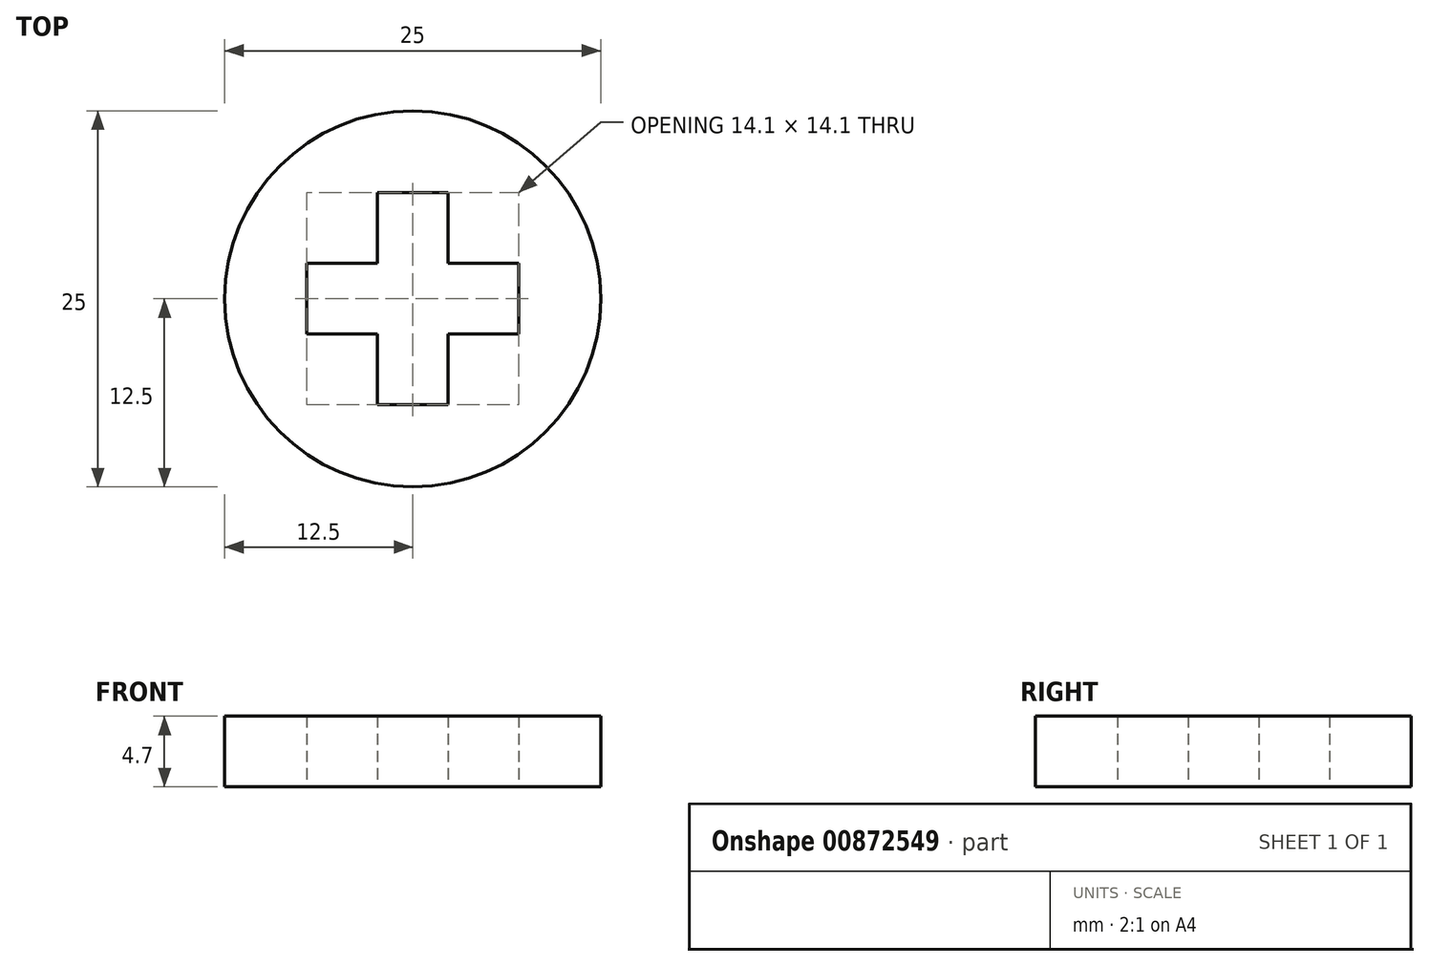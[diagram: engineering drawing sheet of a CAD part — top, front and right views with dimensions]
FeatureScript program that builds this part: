
annotation { "Feature Type Name" : "Feature", "Feature Type Description" : "" }
export const myFeature = defineFeature(function(context is Context, id is Id, definition is map)
    precondition{}
    {
        {
            assignVariable(context, id + "F0", {"name" : "e", "anyValue" : 4.7});
        }
        {
            var Q0;
            Q0=qCreatedBy(makeId("Top.planeOp"),FACE);
            var sketch = newSketch(context, id + "F1", { "sketchPlane" : qUnion([Q0])});
            skCircle(sketch, "E0", {"center": v(0, 0) * mm, "radius": 12.5 * mm});
            skLineSegment(sketch, "E1", {"start": v(-7.05, 2.35) * mm, "end": v(-7.05, -2.35) * mm});
            skLineSegment(sketch, "E2", {"start": v(-31.45, 0) * mm, "end": v(18.7, 0) * mm, "construction": true});
            skPoint(sketch, "E3", {"position": v(-7.05, 0) * mm});
            skLineSegment(sketch, "E4", {"start": v(-7.05, 2.35) * mm, "end": v(-2.35, 2.35) * mm});
            skLineSegment(sketch, "E5", {"start": v(-2.35, 2.35) * mm, "end": v(-2.35, 7.05) * mm});
            skLineSegment(sketch, "E6", {"start": v(-2.35, 7.05) * mm, "end": v(2.35, 7.05) * mm});
            skLineSegment(sketch, "E7", {"start": v(2.35, 7.05) * mm, "end": v(2.35, 2.35) * mm});
            skLineSegment(sketch, "E8", {"start": v(2.35, 2.35) * mm, "end": v(7.05, 2.35) * mm});
            skLineSegment(sketch, "E9", {"start": v(7.05, 2.35) * mm, "end": v(7.05, -2.35) * mm});
            skLineSegment(sketch, "E10", {"start": v(7.05, -2.35) * mm, "end": v(2.35, -2.35) * mm});
            skLineSegment(sketch, "E11", {"start": v(2.35, -2.35) * mm, "end": v(2.35, -7.05) * mm});
            skLineSegment(sketch, "E12", {"start": v(2.35, -7.05) * mm, "end": v(-2.35, -7.05) * mm});
            skLineSegment(sketch, "E13", {"start": v(-2.35, -7.05) * mm, "end": v(-2.35, -2.35) * mm});
            skLineSegment(sketch, "E14", {"start": v(-2.35, -2.35) * mm, "end": v(-7.05, -2.35) * mm});
            skLineSegment(sketch, "E15", {"start": v(0, 18.04) * mm, "end": v(0, 7.05) * mm, "construction": true});
            skLineSegment(sketch, "E16", {"start": v(0, 7.05) * mm, "end": v(0, -17.01) * mm, "construction": true});
            skSolve(sketch);
        }
        {
            var Q0;
            Q0=makeQuery(id+"F1.imprint","IMPRINT",FACE,{"disambiguationData":[TD([[makeQuery(id+"F1.imprint","IMPRINT",EDGE,{"derivedFrom":sQuery(id+"F1.wireOp",EDGE,"E0")}),1.0]])]});
            extrude(context, id + "F2", {"entities" : qUnion([Q0]), "depth" : (getVariable(context, 'e')) * mm, "offsetDistance" : 25 * mm});
        }
    });
